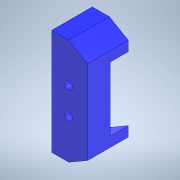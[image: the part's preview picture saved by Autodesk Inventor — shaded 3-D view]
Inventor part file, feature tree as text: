
AUTODESK INVENTOR PART (.ipt)
format: ipt  version: 2022 (Build 260153000, 153)  size: 120,832 bytes
history: native  units: in
note: dims shown in document units (in); Inventor stores cm internally (conversion verified against a paired STEP export)
features: extrude x2
ambient origin geometry x8: Origin, YZ Plane, XZ Plane, XY Plane, X Axis, Y Axis, Z Axis, Center Point
bodies: Solid1 (feature_tree)
feature tree (2):
  extrude  "Extrusion1"  Depth=0.374in
  extrude  "Extrusion2"  Depth=0.1063in
